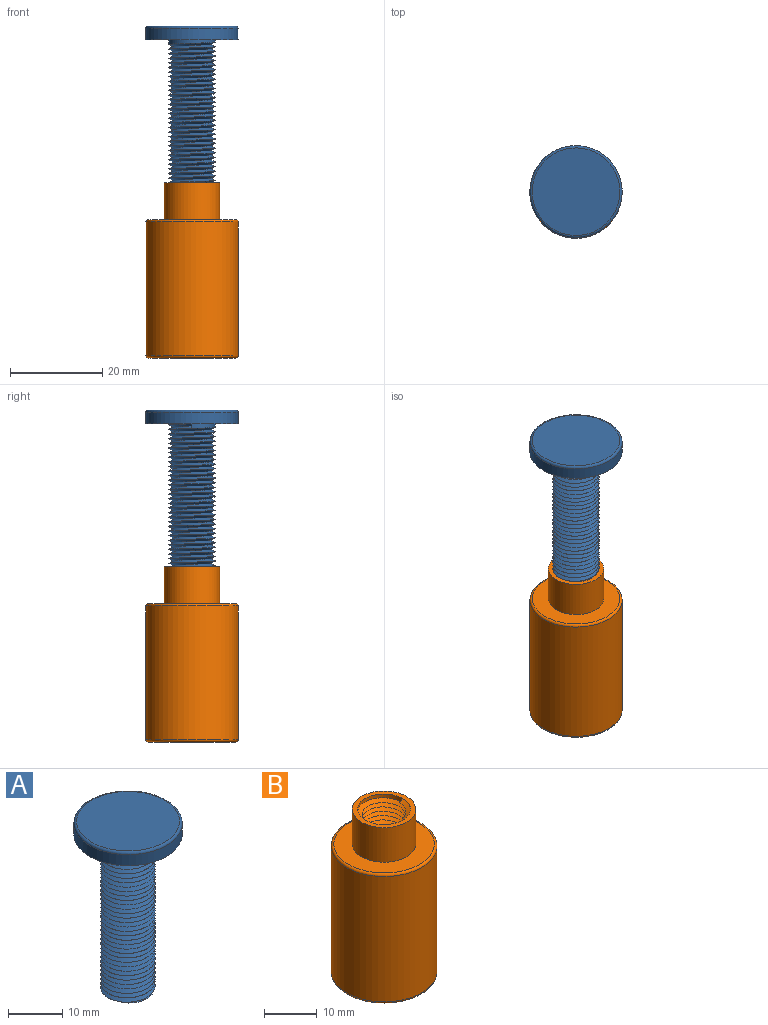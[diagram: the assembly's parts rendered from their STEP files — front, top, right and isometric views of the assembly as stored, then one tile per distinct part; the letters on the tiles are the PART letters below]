
ASSEMBLY  parts=2 mates=1
PART A: 9 faces, bbox 22.4x22.4x39.4 mm
  f0: cylinder r=5mm len=35mm, axis (0,0,1), area 258.5mm2, adj f1,f4,f6,f7,f8
  f1: plane 9.87x9.86mm, normal (0,0,-1), area 65.7mm2, adj f0,f6,f7
  f2: cylinder r=10mm len=20mm, axis (0,0,-1), area 157.1mm2, adj f4,f5
  f3: plane 19x19mm, normal (0,0,1), area 283.5mm2, adj f5
  f4: plane 20x20mm, normal (0,0,-1), area 235.6mm2, adj f0,f2
  f5: torus R=9.5mm, axis (0,0,1), area 48.5mm2, adj f2,f3
  f6: bspline ~35.5x11.55mm, area 1001.3mm2, adj f0,f1,f7,f8
  f7: bspline ~35.17x11.55mm, area 983.4mm2, adj f0,f1,f6,f8
  f8: plane 1x0.87mm, normal (0,-1,0), area 0.4mm2, adj f0,f6,f7
PART B: 16 faces, bbox 22.4x22.4x38.7 mm
  f0: cylinder r=10mm len=29mm, axis (0,0,-1), area 1822.1mm2, adj f5,f6
  f1: plane 19x19mm, normal (0,0,-1), area 252.8mm2, adj f6,f9,f10,f11,f12
  f2: cylinder r=6mm len=12mm, axis (0,0,1), area 301.6mm2, adj f3,f4
  f3: plane 19x19mm, normal (0,0,1), area 170.4mm2, adj f2,f5
  f4: plane 12x12mm, normal (0,0,1), area 34.6mm2, adj f2,f7
  f5: torus R=9.5mm, axis (0,0,1), area 48.5mm2, adj f0,f3
  f6: torus R=9.5mm, axis (0,0,1), area 48.5mm2, adj f0,f1
  f7: cylinder r=5mm len=35mm, axis (0,0,1), area 258.5mm2, adj f4,f8,f13,f14,f15
  f8: plane 9.87x9.86mm, normal (0,0,1), area 35.1mm2, adj f7,f9,f10,f11,f12,f14,f15
  f9: cylinder r=2.83mm len=5mm, axis (0,0,-1), area 18.4mm2, adj f1,f8,f10,f12
  f10: plane 4x3mm, normal (0,1,0), area 12mm2, adj f1,f8,f9,f11
  f11: cylinder r=2.83mm len=5mm, axis (0,0,-1), area 18.4mm2, adj f1,f8,f10,f12
  f12: plane 4x3mm, normal (0,-1,0), area 12mm2, adj f1,f8,f9,f11
  f13: plane 1x0.87mm, normal (0,1,0), area 0.4mm2, adj f7,f14,f15
  f14: bspline ~35.5x11.55mm, area 1001.3mm2, adj f7,f8,f13,f15
  f15: bspline ~35.17x11.55mm, area 983.4mm2, adj f7,f8,f13,f14
PLACE A rot(axis=(0,0,1),180deg) t=(0,0,31)mm
PLACE B at identity fixed
MATE cylindrical A.f0 <-> B.f2  axis (0,0,-1) through (0,0,34)mm
